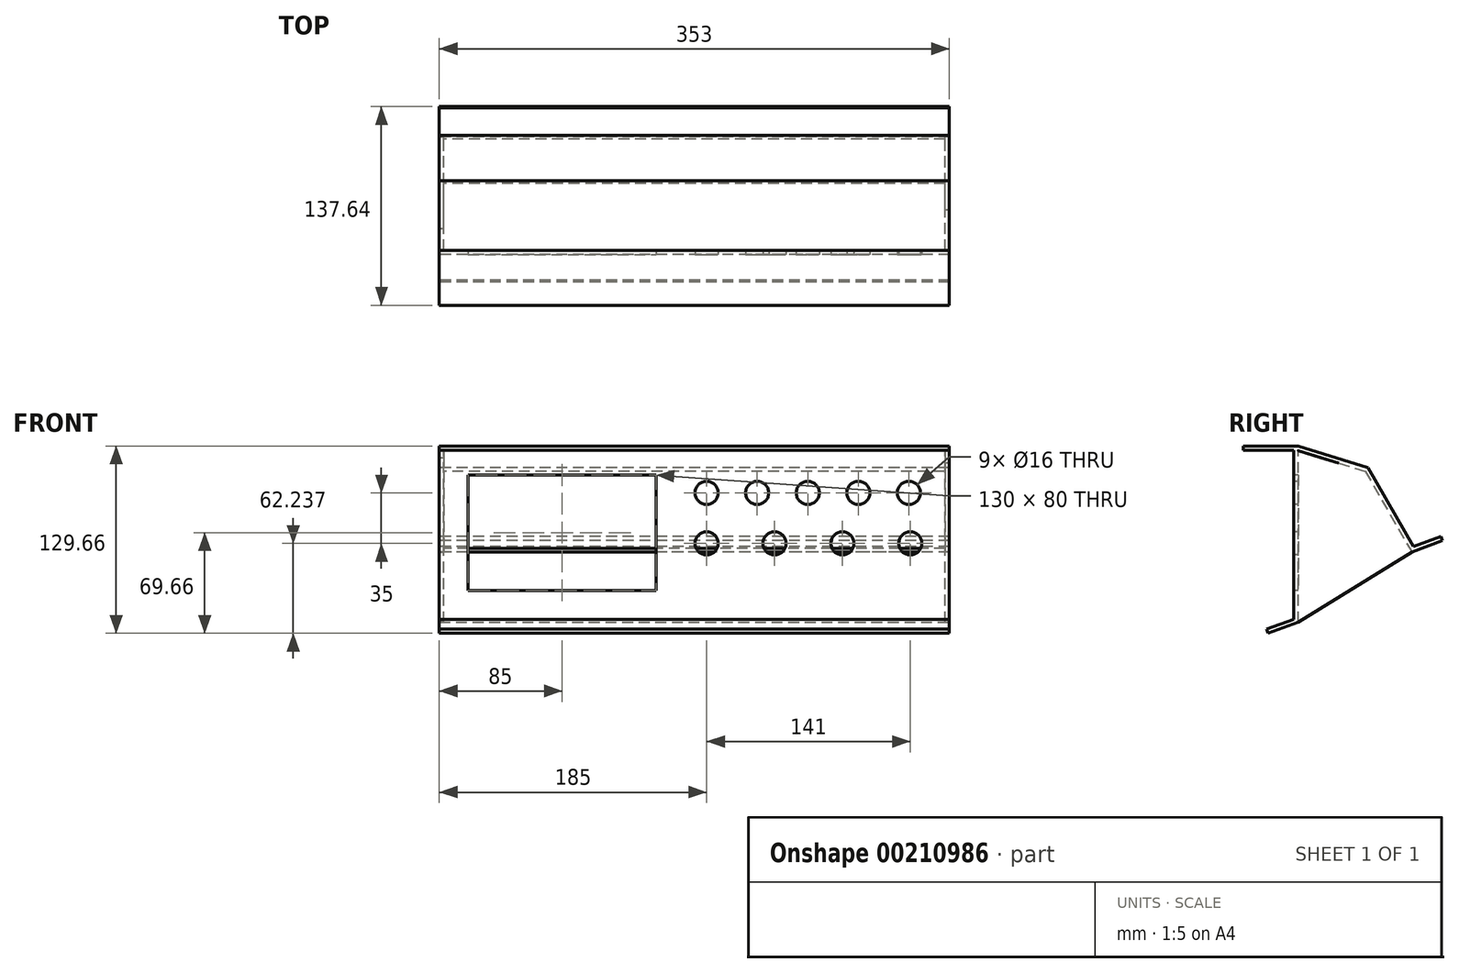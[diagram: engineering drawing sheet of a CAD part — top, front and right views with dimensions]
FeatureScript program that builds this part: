
annotation { "Feature Type Name" : "Feature", "Feature Type Description" : "" }
export const myFeature = defineFeature(function(context is Context, id is Id, definition is map)
    precondition{}
    {
        {
            var Q0;
            Q0=qCreatedBy(makeId("Front.planeOp"),FACE);
            var sketch = newSketch(context, id + "F0", { "sketchPlane" : qUnion([Q0])});
            skCircle(sketch, "E0", {"center": v(8.5, 67.58) * mm, "radius": 8 * mm});
            skCircle(sketch, "E1.1.0.0", {"center": v(43.5, 67.58) * mm, "radius": 8 * mm});
            skCircle(sketch, "E1.2.0.0", {"center": v(78.5, 67.58) * mm, "radius": 8 * mm});
            skCircle(sketch, "E1.3.0.0", {"center": v(113.5, 67.58) * mm, "radius": 8 * mm});
            skCircle(sketch, "E1.4.0.0", {"center": v(148.5, 67.58) * mm, "radius": 8 * mm});
            skLineSegment(sketch, "E1.direction1", {"start": v(8.5, 67.58) * mm, "end": v(43.5, 67.58) * mm, "construction": true});
            skCircle(sketch, "E2", {"center": v(8.5, 32.58) * mm, "radius": 8 * mm});
            skLineSegment(sketch, "E3.bottom", {"start": v(-176.5, 100) * mm, "end": v(176.5, 100) * mm});
            skLineSegment(sketch, "E3.top", {"start": v(-176.5, -20) * mm, "end": v(176.5, -20) * mm});
            skLineSegment(sketch, "E3.left", {"start": v(-176.5, 100) * mm, "end": v(-176.5, -20) * mm});
            skLineSegment(sketch, "E3.right", {"start": v(176.5, 100) * mm, "end": v(176.5, -20) * mm});
            skLineSegment(sketch, "E4.bottom", {"start": v(-156.5, 80) * mm, "end": v(-26.5, 80) * mm});
            skLineSegment(sketch, "E4.top", {"start": v(-156.5, 0) * mm, "end": v(-26.5, 0) * mm});
            skLineSegment(sketch, "E4.left", {"start": v(-156.5, 80) * mm, "end": v(-156.5, 0) * mm});
            skLineSegment(sketch, "E4.right", {"start": v(-26.5, 80) * mm, "end": v(-26.5, 0) * mm});
            skCircle(sketch, "E5.1.0.0", {"center": v(55.5, 32.58) * mm, "radius": 8 * mm});
            skCircle(sketch, "E5.2.0.0", {"center": v(102.5, 32.58) * mm, "radius": 8 * mm});
            skCircle(sketch, "E5.3.0.0", {"center": v(149.5, 32.58) * mm, "radius": 8 * mm});
            skLineSegment(sketch, "E5.direction1", {"start": v(8.5, 32.58) * mm, "end": v(55.5, 32.58) * mm, "construction": true});
            skSolve(sketch);
        }
        {
            var Q0;
            Q0=qCreatedBy(makeId("Right.planeOp"),FACE);
            var sketch = newSketch(context, id + "F1", { "sketchPlane" : qUnion([Q0])});
            skLineSegment(sketch, "E6", {"start": v(0, 0) * mm, "end": v(0, 100) * mm});
            skLineSegment(sketch, "E7", {"start": v(51.3, 85) * mm, "end": v(82.82, 30.49) * mm});
            skLineSegment(sketch, "E8.bottom", {"start": v(0, 100) * mm, "end": v(-35, 100) * mm});
            skLineSegment(sketch, "E8.top", {"start": v(0, 97) * mm, "end": v(-35, 97) * mm});
            skLineSegment(sketch, "E8.left", {"start": v(0, 100) * mm, "end": v(0, 97) * mm});
            skLineSegment(sketch, "E8.right", {"start": v(-35, 100) * mm, "end": v(-35, 97) * mm});
            skLineSegment(sketch, "E9", {"start": v(82.82, 30.49) * mm, "end": v(101.62, 37.33) * mm});
            skLineSegment(sketch, "E10", {"start": v(102.64, 34.5) * mm, "end": v(101.62, 37.33) * mm});
            skLineSegment(sketch, "E11", {"start": v(3, 96.84) * mm, "end": v(49.3, 82.47) * mm});
            skLineSegment(sketch, "E12", {"start": v(3, 96.84) * mm, "end": v(3, -2.1) * mm});
            skLineSegment(sketch, "E13", {"start": v(0, 0) * mm, "end": v(0, -20) * mm});
            skLineSegment(sketch, "E14", {"start": v(0, -20) * mm, "end": v(-18.8, -26.84) * mm});
            skLineSegment(sketch, "E15", {"start": v(-18.8, -26.84) * mm, "end": v(-17.77, -29.66) * mm});
            skLineSegment(sketch, "E16", {"start": v(-17.77, -29.66) * mm, "end": v(3, -22.1) * mm});
            skLineSegment(sketch, "E17", {"start": v(3, -22.1) * mm, "end": v(3, -2.1) * mm});
            skLineSegment(sketch, "E18", {"start": v(3, 96.84) * mm, "end": v(0, 97) * mm});
            skLineSegment(sketch, "E19", {"start": v(3, -22.1) * mm, "end": v(81.79, 26.47) * mm});
            skLineSegment(sketch, "E20", {"start": v(49.3, 82.47) * mm, "end": v(80.23, 28.98) * mm});
            skLineSegment(sketch, "E21", {"start": v(80.23, 28.98) * mm, "end": v(81.79, 26.42) * mm});
            skLineSegment(sketch, "E22", {"start": v(81.79, 26.47) * mm, "end": v(102.64, 34.5) * mm});
            skLineSegment(sketch, "E23", {"start": v(51.3, 85) * mm, "end": v(3, 100) * mm});
            skLineSegment(sketch, "E24", {"start": v(0, 100) * mm, "end": v(3, 100) * mm});
            skLineSegment(sketch, "E25", {"start": v(0, -20) * mm, "end": v(3, -20) * mm});
            skSolve(sketch);
        }
        {
            var Q0;
            Q0=makeQuery(id+"F0.imprint","IMPRINT",FACE,{"disambiguationData":[TD([[makeQuery(id+"F0.imprint","IMPRINT",EDGE,{"derivedFrom":sQuery(id+"F0.wireOp",EDGE,"E0")}),-1.0]])]});
            extrude(context, id + "F2", {"entities" : qUnion([Q0]), "oppositeDirection" : true, "depth" : 3 * mm});
        }
        {
            var Q0;
            Q0=makeQuery(id+"F1.imprint","IMPRINT",FACE,{"disambiguationData":[TD([[makeQuery(id+"F1.imprint","IMPRINT",EDGE,{"derivedFrom":sQuery(id+"F1.wireOp",EDGE,"E14")}),1.0]])]});
            var Q1;
            Q1=makeQuery(id+"F1.imprint","IMPRINT",FACE,{"disambiguationData":[TD([[makeQuery(id+"F1.imprint","IMPRINT",EDGE,{"derivedFrom":sQuery(id+"F1.wireOp",EDGE,"E7")}),-1.0]])]});
            var Q2;
            Q2=makeQuery(id+"F1.imprint","IMPRINT",FACE,{"disambiguationData":[TD([[makeQuery(id+"F1.imprint","IMPRINT",EDGE,{"derivedFrom":sQuery(id+"F1.wireOp",EDGE,"E8.bottom")}),1.0]])]});
            extrude(context, id + "F3", {"entities" : qUnion([Q0, Q1, Q2]), "operationType" : NewBodyOperationType.ADD, "endBound" : BoundingType.SYMMETRIC, "depth" : 353 * mm});
        }
        {
            var Q0;
            Q0=qCreatedBy(makeId("Right.planeOp"),FACE);
            cPlane(context, id + "F4", {"entities" : qUnion([Q0]), "cplaneType" : CPlaneType.OFFSET, "offset" : 176.5 * mm, "width" : 150 * mm, "height" : 150 * mm});
        }
        {
            var Q0;
            Q0=qCreatedBy(id+"F4.planeOp",FACE);
            var sketch = newSketch(context, id + "F5", { "sketchPlane" : qUnion([Q0])});
            skLineSegment(sketch, "E26", {"start": v(3, 96.8) * mm, "end": v(49.32, 82.48) * mm});
            skLineSegment(sketch, "E27", {"start": v(3, 96.8) * mm, "end": v(3, -22.1) * mm});
            skLineSegment(sketch, "E28", {"start": v(3, -22.1) * mm, "end": v(81.75, 26.5) * mm});
            skLineSegment(sketch, "E29", {"start": v(49.32, 82.48) * mm, "end": v(81.75, 26.5) * mm});
            skSolve(sketch);
        }
        {
            var Q0;
            Q0=makeQuery(id+"F5.imprint","IMPRINT",FACE,{"disambiguationData":[TD([[makeQuery(id+"F5.imprint","IMPRINT",EDGE,{"derivedFrom":sQuery(id+"F5.wireOp",EDGE,"E26")}),-1.0]])]});
            extrude(context, id + "F6", {"entities" : qUnion([Q0]), "operationType" : NewBodyOperationType.ADD, "oppositeDirection" : true, "depth" : 3 * mm});
        }
        {
            var Q0;
            Q0=qCreatedBy(id+"F4.planeOp",FACE);
            cPlane(context, id + "F7", {"entities" : qUnion([Q0]), "cplaneType" : CPlaneType.OFFSET, "offset" : 353 * mm, "oppositeDirection" : true, "width" : 150 * mm, "height" : 150 * mm});
        }
        {
            var Q0;
            Q0=qCreatedBy(id+"F7.planeOp",FACE);
            var sketch = newSketch(context, id + "F8", { "sketchPlane" : qUnion([Q0])});
            skLineSegment(sketch, "E30", {"start": v(2.98, 96.83) * mm, "end": v(49.3, 82.5) * mm});
            skLineSegment(sketch, "E31", {"start": v(2.98, 96.83) * mm, "end": v(2.98, -22.07) * mm});
            skLineSegment(sketch, "E32", {"start": v(2.98, -22.07) * mm, "end": v(81.73, 26.52) * mm});
            skLineSegment(sketch, "E33", {"start": v(49.3, 82.5) * mm, "end": v(81.73, 26.52) * mm});
            skSolve(sketch);
        }
        {
            var Q0;
            Q0=makeQuery(id+"F8.imprint","IMPRINT",FACE,{"disambiguationData":[TD([[makeQuery(id+"F8.imprint","IMPRINT",EDGE,{"derivedFrom":sQuery(id+"F8.wireOp",EDGE,"E30")}),-1.0]])]});
            extrude(context, id + "F9", {"entities" : qUnion([Q0]), "operationType" : NewBodyOperationType.ADD, "depth" : 3 * mm});
        }
    });
